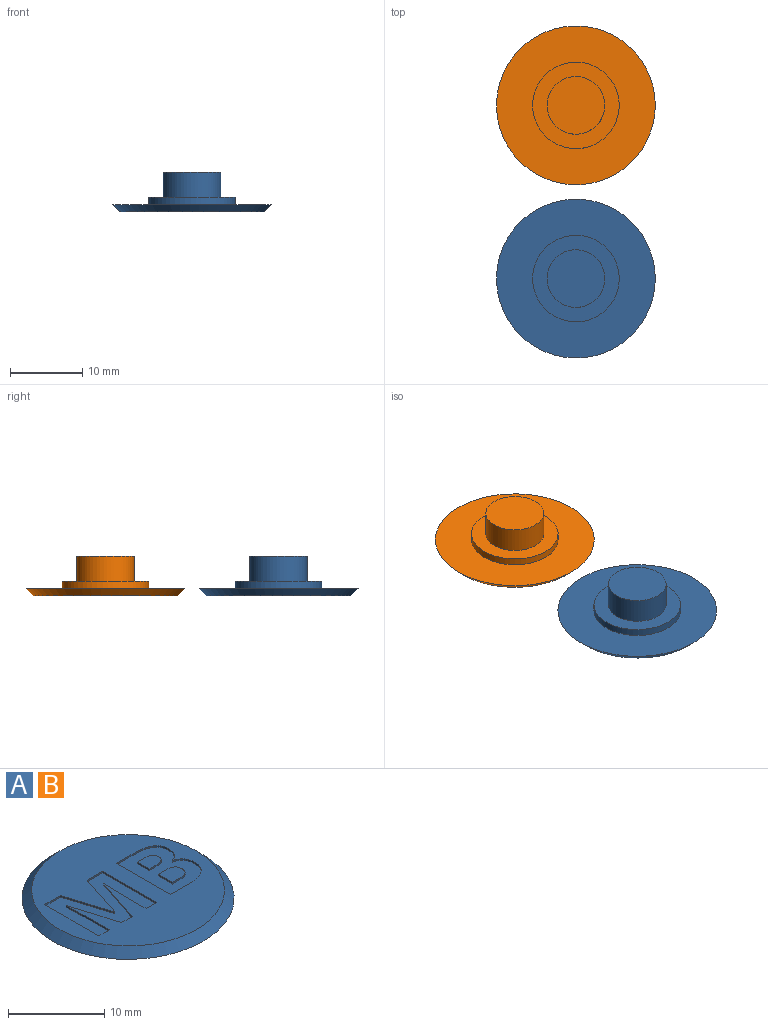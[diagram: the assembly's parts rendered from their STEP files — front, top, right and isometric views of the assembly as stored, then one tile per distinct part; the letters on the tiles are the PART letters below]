
ASSEMBLY  parts=2 mates=1
PART A: 55 faces, bbox 22x22x5.5 mm
  f0: plane 20x20mm, normal (0,0,1), area 228.2mm2, adj f6,f7,f8,f9,f10,f11,f12,f13
  f1: cylinder r=4mm len=8mm, axis (0,0,-1), area 88mm2, adj f2,f4
  f2: plane 8x8mm, normal (0,0,-1), area 50.3mm2, adj f1
  f3: cylinder r=6mm len=12mm, axis (0,0,-1), area 37.7mm2, adj f4,f5
  f4: plane 12x12mm, normal (0,0,-1), area 62.8mm2, adj f1,f3
  f5: plane 22x22mm, normal (0,0,-1), area 267mm2, adj f3,f54
  f6: plane 1.54x0.2mm, normal (0,1,0), area 0.3mm2, adj f0,f7,f24,f25
  f7: plane 6.21x2.05mm, normal (-0.95,0.31,0), area 1.3mm2, adj f0,f6,f8,f25
  f8: plane 0.2x0.05mm, normal (0,1,0), area 0mm2, adj f0,f7,f9,f25
  f9: extruded ~1.84x0.2mm, area 0.4mm2, adj f0,f8,f10,f25
  f10: extruded ~0.61x0.2mm, area 0.1mm2, adj f0,f9,f11,f25
  f11: plane 3.76x0.2mm, normal (1,0,0), area 0.8mm2, adj f0,f10,f12,f25
  f12: plane 1.57x0.2mm, normal (0,1,0), area 0.3mm2, adj f0,f11,f13,f25
  f13: plane 7.93x0.2mm, normal (-1,0,0), area 1.6mm2, adj f0,f12,f14,f25
  f14: plane 2.29x0.2mm, normal (0,-1,0), area 0.5mm2, adj f0,f13,f15,f25
  f15: plane 6.07x1.99mm, normal (0.95,-0.31,0), area 1.3mm2, adj f0,f14,f16,f25
  f16: plane 0.2x0.03mm, normal (0,-1,0), area 0mm2, adj f0,f15,f17,f25
  f17: plane 6.07x1.88mm, normal (-0.96,-0.3,0), area 1.3mm2, adj f0,f16,f18,f25
  f18: plane 2.29x0.2mm, normal (0,-1,0), area 0.5mm2, adj f0,f17,f19,f25
  f19: plane 7.93x0.2mm, normal (1,0,0), area 1.6mm2, adj f0,f18,f20,f25
  f20: plane 1.5x0.2mm, normal (0,1,0), area 0.3mm2, adj f0,f19,f21,f25
  f21: plane 3.69x0.2mm, normal (-1,0,0), area 0.7mm2, adj f0,f20,f22,f25
  f22: extruded ~2.53x0.2mm, area 0.5mm2, adj f0,f21,f23,f25
  f23: plane 0.2x0.05mm, normal (0,1,0), area 0mm2, adj f0,f22,f24,f25
  f24: plane 6.22x1.91mm, normal (0.96,0.29,0), area 1.3mm2, adj f0,f6,f23,f25
  f25: plane 8.48x7.93mm, normal (0,0,1), area 43.4mm2, adj f6,f7,f8,f9,f10,f11,f12,f13
  f26: plane 7.93x0.2mm, normal (1,0,0), area 1.6mm2, adj f0,f27,f50,f51
  f27: plane 2.97x0.2mm, normal (0,1,0), area 0.6mm2, adj f0,f26,f28,f51
  f28: extruded ~2.13x0.61mm, area 0.5mm2, adj f0,f27,f29,f51
  f29: extruded ~1.69x0.78mm, area 0.4mm2, adj f0,f28,f30,f51
  f30: extruded ~1.23x0.33mm, area 0.3mm2, adj f0,f29,f31,f51
  f31: extruded ~1.09x0.63mm, area 0.3mm2, adj f0,f30,f32,f51
  f32: plane 0.2x0.05mm, normal (-1,0,0), area 0mm2, adj f0,f31,f33,f51
  f33: extruded ~0.89x0.55mm, area 0.2mm2, adj f0,f32,f34,f51
  f34: extruded ~1.17x0.33mm, area 0.2mm2, adj f0,f33,f35,f51
  f35: extruded ~1.53x0.76mm, area 0.4mm2, adj f0,f34,f36,f51
  f36: extruded ~2.45x0.48mm, area 0.5mm2, adj f0,f35,f50,f51
  f37: plane 1.76x0.2mm, normal (-1,0,0), area 0.4mm2, adj f38,f48,f51,f53
  f38: plane 0.88x0.2mm, normal (0,1,0), area 0.2mm2, adj f37,f39,f51,f53
  f39: extruded ~1.06x0.2mm, area 0.2mm2, adj f38,f40,f51,f53
  f40: extruded ~0.65x0.33mm, area 0.2mm2, adj f39,f41,f51,f53
  f41: extruded ~0.7x0.31mm, area 0.2mm2, adj f40,f42,f51,f53
  f42: extruded ~0.99x0.21mm, area 0.2mm2, adj f41,f48,f51,f53
  f43: plane 1.04x0.2mm, normal (0,1,0), area 0.2mm2, adj f44,f49,f51,f52
  f44: extruded ~1.41x0.99mm, area 0.4mm2, adj f43,f45,f51,f52
  f45: extruded ~0.81x0.33mm, area 0.2mm2, adj f44,f46,f51,f52
  f46: extruded ~1.03x0.27mm, area 0.2mm2, adj f45,f47,f51,f52
  f47: plane 1.1x0.2mm, normal (0,-1,0), area 0.2mm2, adj f46,f49,f51,f52
  f48: plane 0.98x0.2mm, normal (0,-1,0), area 0.2mm2, adj f37,f42,f51,f53
  f49: plane 2.07x0.2mm, normal (-1,0,0), area 0.4mm2, adj f43,f47,f51,f52
  f50: plane 2.47x0.2mm, normal (0,-1,0), area 0.5mm2, adj f0,f26,f36,f51
  f51: plane 7.93x5.88mm, normal (0,0,1), area 34.3mm2, adj f26,f27,f28,f29,f30,f31,f32,f33
  f52: plane 2.45x2.07mm, normal (0,0,1), area 4.6mm2, adj f43,f44,f45,f46,f47,f49
  f53: plane 2.27x1.76mm, normal (0,0,1), area 3.6mm2, adj f37,f38,f39,f40,f41,f42,f48
  f54: cone r=10mm half-angle=45deg, axis (0,0,-1), area 93.3mm2, adj f0,f5
PART B: same geometry as A
PLACE A rot(axis=(-1,0,0),180deg) t=(-6.81,-19.89,12.97)mm
PLACE B rot(axis=(-1,0,0),180deg) t=(-6.81,4.11,12.97)mm fixed
MATE parallel B.f1 <-> A.f1  axis (0,0,1) through (-6.81,4.11,12.97)mm
